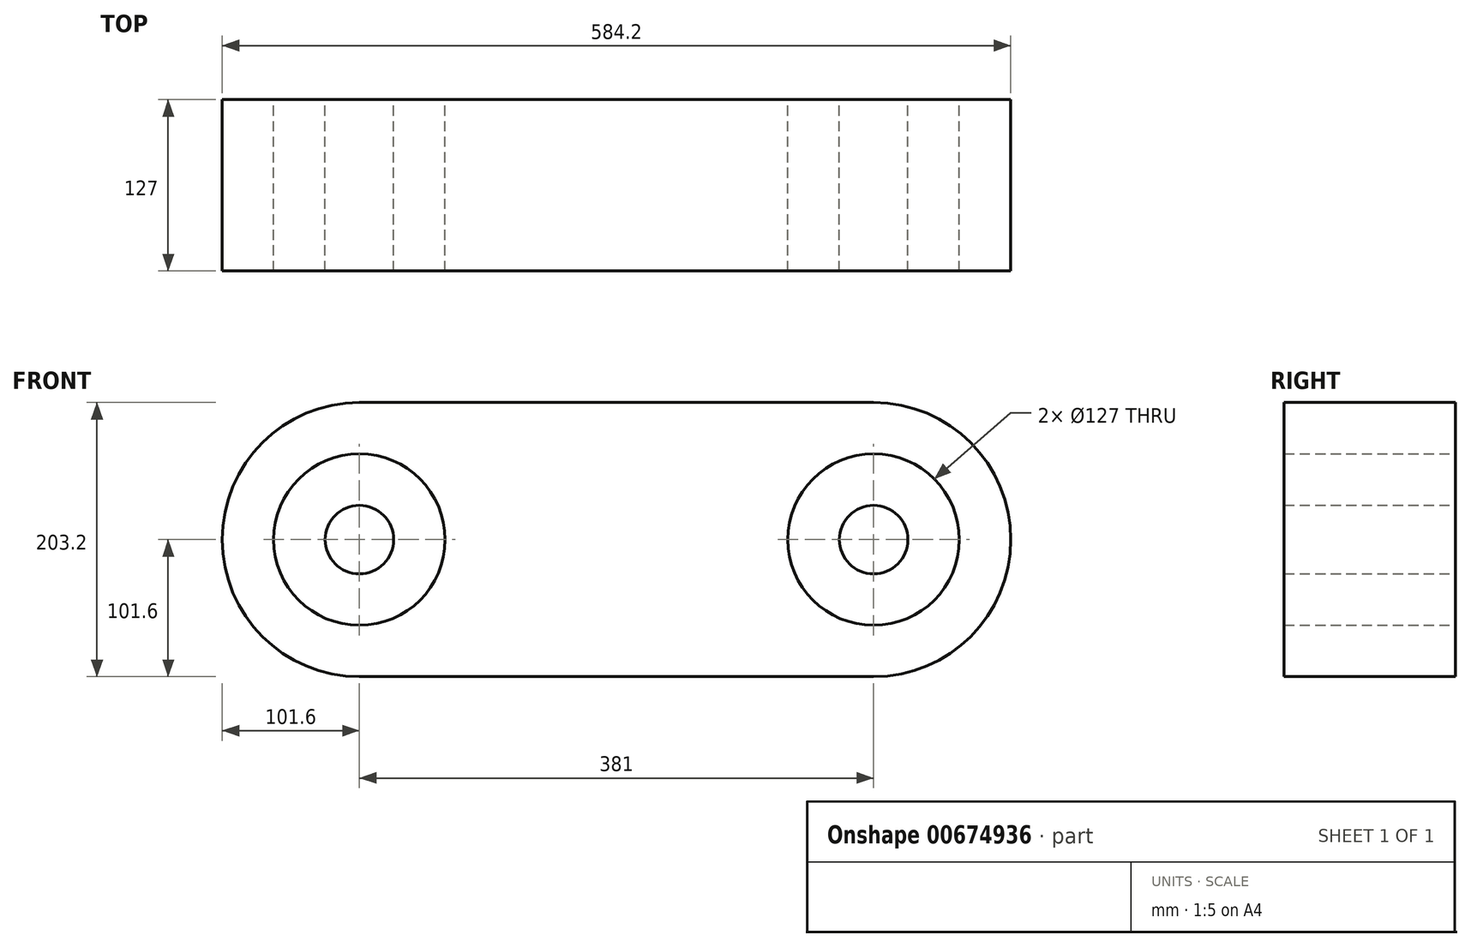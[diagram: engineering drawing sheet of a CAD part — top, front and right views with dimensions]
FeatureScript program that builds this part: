
annotation { "Feature Type Name" : "Feature", "Feature Type Description" : "" }
export const myFeature = defineFeature(function(context is Context, id is Id, definition is map)
    precondition{}
    {
        {
            var Q0;
            Q0=qCreatedBy(makeId("Front.planeOp"),FACE);
            var sketch = newSketch(context, id + "F0", { "sketchPlane" : qUnion([Q0])});
            skLineSegment(sketch, "E0.bottom", {"start": v(0, 0) * mm, "end": v(381, 0) * mm});
            skLineSegment(sketch, "E0.top", {"start": v(0, 203.2) * mm, "end": v(381, 203.2) * mm});
            skArc(sketch, "E1", {"start": v(0, 0) * mm, "mid": v(-101.6, 101.6) * mm, "end": v(0, 203.2) * mm});
            skArc(sketch, "E2", {"start": v(381, 0) * mm, "mid": v(482.6, 101.6) * mm, "end": v(381, 203.2) * mm});
            skCircle(sketch, "E3", {"center": v(0, 101.6) * mm, "radius": 63.5 * mm});
            skCircle(sketch, "E4", {"center": v(381, 101.6) * mm, "radius": 63.5 * mm});
            skCircle(sketch, "E5", {"center": v(381, 101.6) * mm, "radius": 25.4 * mm});
            skCircle(sketch, "E6", {"center": v(0, 101.6) * mm, "radius": 25.4 * mm});
            skSolve(sketch);
        }
        {
            var Q0;
            Q0=makeQuery(id+"F0.imprint","IMPRINT",FACE,{"disambiguationData":[TD([[makeQuery(id+"F0.imprint","IMPRINT",EDGE,{"derivedFrom":sQuery(id+"F0.wireOp",EDGE,"E0.bottom")}),1.0]])]});
            var Q1;
            Q1=makeQuery(id+"F0.imprint","IMPRINT",FACE,{"disambiguationData":[TD([[makeQuery(id+"F0.imprint","IMPRINT",EDGE,{"derivedFrom":sQuery(id+"F0.wireOp",EDGE,"E6")}),1.0]])]});
            var Q2;
            Q2=makeQuery(id+"F0.imprint","IMPRINT",FACE,{"disambiguationData":[TD([[makeQuery(id+"F0.imprint","IMPRINT",EDGE,{"derivedFrom":sQuery(id+"F0.wireOp",EDGE,"E5")}),1.0]])]});
            extrude(context, id + "F1", {"entities" : qUnion([Q0, Q1, Q2]), "depth" : 127 * mm, "offsetDistance" : 25.4 * mm});
        }
    });
